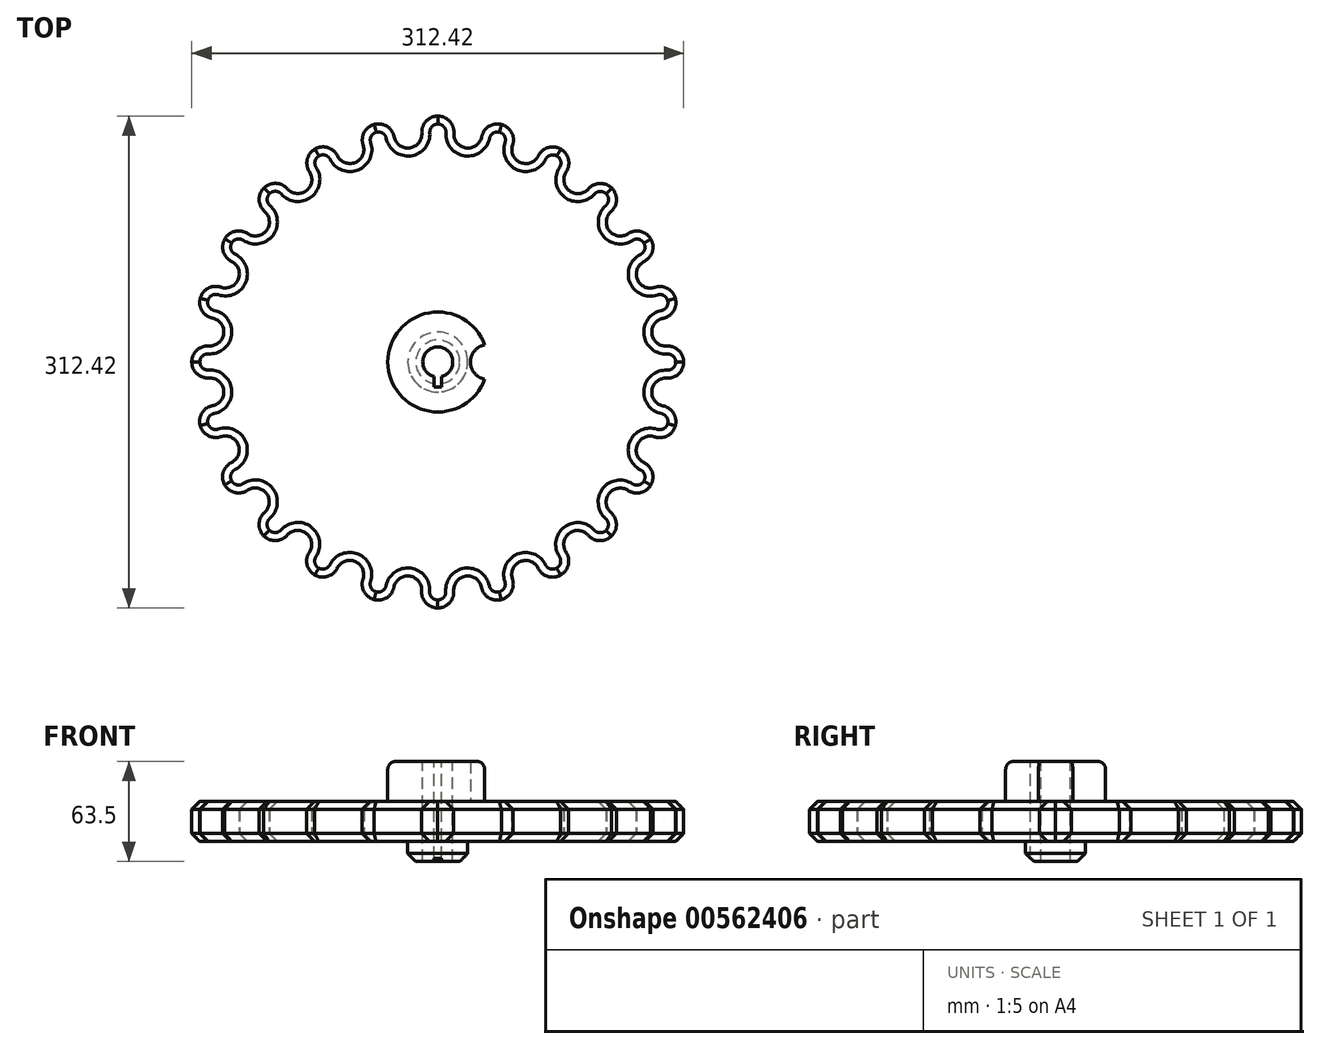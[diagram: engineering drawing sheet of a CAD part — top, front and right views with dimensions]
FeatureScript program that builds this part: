
annotation { "Feature Type Name" : "Feature", "Feature Type Description" : "" }
export const myFeature = defineFeature(function(context is Context, id is Id, definition is map)
    precondition{}
    {
        {
            var Q0;
            Q0=qCreatedBy(makeId("Top.planeOp"),FACE);
            var sketch = newSketch(context, id + "F0", { "sketchPlane" : qUnion([Q0])});
            skCircle(sketch, "E0", {"center": v(0, 0) * mm, "radius": 146.05 * mm, "construction": true});
            skArc(sketch, "E1", {"start": v(145.34, -10.14) * mm, "mid": v(156.2, -0.02) * mm, "end": v(145.39, 10.14) * mm});
            skArc(sketch, "E2", {"start": v(143.08, 27.73) * mm, "mid": v(150.91, 40.34) * mm, "end": v(137.8, 47.3) * mm});
            skArc(sketch, "E3", {"start": v(143.38, 27.78) * mm, "mid": v(136, 17.85) * mm, "end": v(145.7, 10.16) * mm});
            skLineSegment(sketch, "E4", {"start": v(0, 0) * mm, "end": v(138.14, 47.42) * mm});
            skLineSegment(sketch, "E5", {"start": v(0, 0) * mm, "end": v(145.7, -10.16) * mm});
            skSolve(sketch);
        }
        {
            var Q0;
            Q0 = qSketchRegion(id + "F0", true);
            extrude(context, id + "F1", {"entities" : qUnion([Q0]), "depth" : 25.4 * mm, "offsetDistance" : 25.4 * mm});
        }
        {
            var Q0;
            Q0=makeQuery(id+"F1.opExtrude","SWEPT_BODY",BODY,{"disambiguationData":[OSD([sQuery(id+"F0.wireOp",EDGE,"E1"),sQuery(id+"F0.wireOp",EDGE,"E2"),sQuery(id+"F0.wireOp",EDGE,"E3"),sQuery(id+"F0.wireOp",EDGE,"E4"),sQuery(id+"F0.wireOp",EDGE,"E5")])]});
            var Q1;
            Q1=makeQuery(id+"F1.opExtrude","SWEPT_EDGE",EDGE,{"disambiguationData":[OSD([sQuery(id+"F0.wireOp",EDGE,"E4"),sQuery(id+"F0.wireOp",EDGE,"E5")])]});
            circularPattern(context, id + "F2", {"operationType" : NewBodyOperationType.ADD, "entities" : qUnion([Q0]), "axis" : qUnion([Q1]), "angle" : 360 * degree, "instanceCount" : 24, "oppositeDirection" : true, "equalSpace" : true});
        }
        {
            var Q0;
            {var subQ0=makeQuery(id+"F1.opExtrude","CAP_FACE",FACE,{"disambiguationData":[OSD([sQuery(id+"F0.wireOp",EDGE,"E1"),sQuery(id+"F0.wireOp",EDGE,"E2"),sQuery(id+"F0.wireOp",EDGE,"E3"),sQuery(id+"F0.wireOp",EDGE,"E4"),sQuery(id+"F0.wireOp",EDGE,"E5")])],"isStart":false});Q0=makeQuery(id+"F2.boolean.opBoolean","MERGE",FACE,{"derivedFrom":[subQ0,makeQuery(id+"F2.opPattern","COPY",FACE,{"derivedFrom":subQ0,"instanceName":"1"}),makeQuery(id+"F2.opPattern","COPY",FACE,{"derivedFrom":subQ0,"instanceName":"2"}),makeQuery(id+"F2.opPattern","COPY",FACE,{"derivedFrom":subQ0,"instanceName":"3"}),makeQuery(id+"F2.opPattern","COPY",FACE,{"derivedFrom":subQ0,"instanceName":"4"}),makeQuery(id+"F2.opPattern","COPY",FACE,{"derivedFrom":subQ0,"instanceName":"5"}),makeQuery(id+"F2.opPattern","COPY",FACE,{"derivedFrom":subQ0,"instanceName":"6"}),makeQuery(id+"F2.opPattern","COPY",FACE,{"derivedFrom":subQ0,"instanceName":"7"}),makeQuery(id+"F2.opPattern","COPY",FACE,{"derivedFrom":subQ0,"instanceName":"8"}),makeQuery(id+"F2.opPattern","COPY",FACE,{"derivedFrom":subQ0,"instanceName":"9"}),makeQuery(id+"F2.opPattern","COPY",FACE,{"derivedFrom":subQ0,"instanceName":"10"}),makeQuery(id+"F2.opPattern","COPY",FACE,{"derivedFrom":subQ0,"instanceName":"11"}),makeQuery(id+"F2.opPattern","COPY",FACE,{"derivedFrom":subQ0,"instanceName":"12"}),makeQuery(id+"F2.opPattern","COPY",FACE,{"derivedFrom":subQ0,"instanceName":"13"}),makeQuery(id+"F2.opPattern","COPY",FACE,{"derivedFrom":subQ0,"instanceName":"14"}),makeQuery(id+"F2.opPattern","COPY",FACE,{"derivedFrom":subQ0,"instanceName":"15"}),makeQuery(id+"F2.opPattern","COPY",FACE,{"derivedFrom":subQ0,"instanceName":"16"}),makeQuery(id+"F2.opPattern","COPY",FACE,{"derivedFrom":subQ0,"instanceName":"17"}),makeQuery(id+"F2.opPattern","COPY",FACE,{"derivedFrom":subQ0,"instanceName":"18"}),makeQuery(id+"F2.opPattern","COPY",FACE,{"derivedFrom":subQ0,"instanceName":"19"}),makeQuery(id+"F2.opPattern","COPY",FACE,{"derivedFrom":subQ0,"instanceName":"20"}),makeQuery(id+"F2.opPattern","COPY",FACE,{"derivedFrom":subQ0,"instanceName":"21"}),makeQuery(id+"F2.opPattern","COPY",FACE,{"derivedFrom":subQ0,"instanceName":"22"}),makeQuery(id+"F2.opPattern","COPY",FACE,{"derivedFrom":subQ0,"instanceName":"23"})]});}
            var Q1;
            {var subQ0=makeQuery(id+"F1.opExtrude","CAP_FACE",FACE,{"disambiguationData":[OSD([sQuery(id+"F0.wireOp",EDGE,"E1"),sQuery(id+"F0.wireOp",EDGE,"E2"),sQuery(id+"F0.wireOp",EDGE,"E3"),sQuery(id+"F0.wireOp",EDGE,"E4"),sQuery(id+"F0.wireOp",EDGE,"E5")])],"isStart":true});Q1=makeQuery(id+"F2.boolean.opBoolean","MERGE",FACE,{"derivedFrom":[subQ0,makeQuery(id+"F2.opPattern","COPY",FACE,{"derivedFrom":subQ0,"instanceName":"1"}),makeQuery(id+"F2.opPattern","COPY",FACE,{"derivedFrom":subQ0,"instanceName":"2"}),makeQuery(id+"F2.opPattern","COPY",FACE,{"derivedFrom":subQ0,"instanceName":"3"}),makeQuery(id+"F2.opPattern","COPY",FACE,{"derivedFrom":subQ0,"instanceName":"4"}),makeQuery(id+"F2.opPattern","COPY",FACE,{"derivedFrom":subQ0,"instanceName":"5"}),makeQuery(id+"F2.opPattern","COPY",FACE,{"derivedFrom":subQ0,"instanceName":"6"}),makeQuery(id+"F2.opPattern","COPY",FACE,{"derivedFrom":subQ0,"instanceName":"7"}),makeQuery(id+"F2.opPattern","COPY",FACE,{"derivedFrom":subQ0,"instanceName":"8"}),makeQuery(id+"F2.opPattern","COPY",FACE,{"derivedFrom":subQ0,"instanceName":"9"}),makeQuery(id+"F2.opPattern","COPY",FACE,{"derivedFrom":subQ0,"instanceName":"10"}),makeQuery(id+"F2.opPattern","COPY",FACE,{"derivedFrom":subQ0,"instanceName":"11"}),makeQuery(id+"F2.opPattern","COPY",FACE,{"derivedFrom":subQ0,"instanceName":"12"}),makeQuery(id+"F2.opPattern","COPY",FACE,{"derivedFrom":subQ0,"instanceName":"13"}),makeQuery(id+"F2.opPattern","COPY",FACE,{"derivedFrom":subQ0,"instanceName":"14"}),makeQuery(id+"F2.opPattern","COPY",FACE,{"derivedFrom":subQ0,"instanceName":"15"}),makeQuery(id+"F2.opPattern","COPY",FACE,{"derivedFrom":subQ0,"instanceName":"16"}),makeQuery(id+"F2.opPattern","COPY",FACE,{"derivedFrom":subQ0,"instanceName":"17"}),makeQuery(id+"F2.opPattern","COPY",FACE,{"derivedFrom":subQ0,"instanceName":"18"}),makeQuery(id+"F2.opPattern","COPY",FACE,{"derivedFrom":subQ0,"instanceName":"19"}),makeQuery(id+"F2.opPattern","COPY",FACE,{"derivedFrom":subQ0,"instanceName":"20"}),makeQuery(id+"F2.opPattern","COPY",FACE,{"derivedFrom":subQ0,"instanceName":"21"}),makeQuery(id+"F2.opPattern","COPY",FACE,{"derivedFrom":subQ0,"instanceName":"22"}),makeQuery(id+"F2.opPattern","COPY",FACE,{"derivedFrom":subQ0,"instanceName":"23"})]});}
            chamfer(context, id + "F3", {"entities" : qUnion([Q0, Q1]), "width" : 5.08 * mm, "tangentPropagation" : true});
        }
        {
            var Q0;
            {var subQ0=makeQuery(id+"F1.opExtrude","CAP_FACE",FACE,{"disambiguationData":[OSD([sQuery(id+"F0.wireOp",EDGE,"E1"),sQuery(id+"F0.wireOp",EDGE,"E2"),sQuery(id+"F0.wireOp",EDGE,"E3"),sQuery(id+"F0.wireOp",EDGE,"E4"),sQuery(id+"F0.wireOp",EDGE,"E5")])],"isStart":false});Q0=makeQuery(id+"F2.boolean.opBoolean","MERGE",FACE,{"derivedFrom":[subQ0,makeQuery(id+"F2.opPattern","COPY",FACE,{"derivedFrom":subQ0,"instanceName":"1"}),makeQuery(id+"F2.opPattern","COPY",FACE,{"derivedFrom":subQ0,"instanceName":"2"}),makeQuery(id+"F2.opPattern","COPY",FACE,{"derivedFrom":subQ0,"instanceName":"3"}),makeQuery(id+"F2.opPattern","COPY",FACE,{"derivedFrom":subQ0,"instanceName":"4"}),makeQuery(id+"F2.opPattern","COPY",FACE,{"derivedFrom":subQ0,"instanceName":"5"}),makeQuery(id+"F2.opPattern","COPY",FACE,{"derivedFrom":subQ0,"instanceName":"6"}),makeQuery(id+"F2.opPattern","COPY",FACE,{"derivedFrom":subQ0,"instanceName":"7"}),makeQuery(id+"F2.opPattern","COPY",FACE,{"derivedFrom":subQ0,"instanceName":"8"}),makeQuery(id+"F2.opPattern","COPY",FACE,{"derivedFrom":subQ0,"instanceName":"9"}),makeQuery(id+"F2.opPattern","COPY",FACE,{"derivedFrom":subQ0,"instanceName":"10"}),makeQuery(id+"F2.opPattern","COPY",FACE,{"derivedFrom":subQ0,"instanceName":"11"}),makeQuery(id+"F2.opPattern","COPY",FACE,{"derivedFrom":subQ0,"instanceName":"12"}),makeQuery(id+"F2.opPattern","COPY",FACE,{"derivedFrom":subQ0,"instanceName":"13"}),makeQuery(id+"F2.opPattern","COPY",FACE,{"derivedFrom":subQ0,"instanceName":"14"}),makeQuery(id+"F2.opPattern","COPY",FACE,{"derivedFrom":subQ0,"instanceName":"15"}),makeQuery(id+"F2.opPattern","COPY",FACE,{"derivedFrom":subQ0,"instanceName":"16"}),makeQuery(id+"F2.opPattern","COPY",FACE,{"derivedFrom":subQ0,"instanceName":"17"}),makeQuery(id+"F2.opPattern","COPY",FACE,{"derivedFrom":subQ0,"instanceName":"18"}),makeQuery(id+"F2.opPattern","COPY",FACE,{"derivedFrom":subQ0,"instanceName":"19"}),makeQuery(id+"F2.opPattern","COPY",FACE,{"derivedFrom":subQ0,"instanceName":"20"}),makeQuery(id+"F2.opPattern","COPY",FACE,{"derivedFrom":subQ0,"instanceName":"21"}),makeQuery(id+"F2.opPattern","COPY",FACE,{"derivedFrom":subQ0,"instanceName":"22"}),makeQuery(id+"F2.opPattern","COPY",FACE,{"derivedFrom":subQ0,"instanceName":"23"})]});}
            var sketch = newSketch(context, id + "F4", { "sketchPlane" : qUnion([Q0])});
            skArc(sketch, "E6", {"start": v(29.83, 10.88) * mm, "mid": v(-31.75, 0) * mm, "end": v(29.83, -10.88) * mm});
            skArc(sketch, "E7", {"start": v(29.83, 10.88) * mm, "mid": v(20.7, 0) * mm, "end": v(29.83, -10.88) * mm});
            skSolve(sketch);
        }
        {
            var Q0;
            Q0 = qSketchRegion(id + "F4", true);
            extrude(context, id + "F5", {"entities" : qUnion([Q0]), "operationType" : NewBodyOperationType.ADD, "depth" : 25.4 * mm, "offsetDistance" : 25.4 * mm});
        }
        {
            var Q0;
            Q0=makeQuery(id+"F5.opExtrude","CAP_EDGE",EDGE,{"disambiguationData":[OSD([sQuery(id+"F4.wireOp",EDGE,"E6")])],"isStart":false});
            fillet(context, id + "F6", {"entities" : qUnion([Q0]), "radius" : 5.08 * mm, "tangentPropagation" : true, "allowEdgeOverflow" : false});
        }
        {
            var Q0;
            {var subQ0=makeQuery(id+"F1.opExtrude","CAP_FACE",FACE,{"disambiguationData":[OSD([sQuery(id+"F0.wireOp",EDGE,"E1"),sQuery(id+"F0.wireOp",EDGE,"E2"),sQuery(id+"F0.wireOp",EDGE,"E3"),sQuery(id+"F0.wireOp",EDGE,"E4"),sQuery(id+"F0.wireOp",EDGE,"E5")])],"isStart":true});Q0=makeQuery(id+"F2.boolean.opBoolean","MERGE",FACE,{"derivedFrom":[subQ0,makeQuery(id+"F2.opPattern","COPY",FACE,{"derivedFrom":subQ0,"instanceName":"1"}),makeQuery(id+"F2.opPattern","COPY",FACE,{"derivedFrom":subQ0,"instanceName":"2"}),makeQuery(id+"F2.opPattern","COPY",FACE,{"derivedFrom":subQ0,"instanceName":"3"}),makeQuery(id+"F2.opPattern","COPY",FACE,{"derivedFrom":subQ0,"instanceName":"4"}),makeQuery(id+"F2.opPattern","COPY",FACE,{"derivedFrom":subQ0,"instanceName":"5"}),makeQuery(id+"F2.opPattern","COPY",FACE,{"derivedFrom":subQ0,"instanceName":"6"}),makeQuery(id+"F2.opPattern","COPY",FACE,{"derivedFrom":subQ0,"instanceName":"7"}),makeQuery(id+"F2.opPattern","COPY",FACE,{"derivedFrom":subQ0,"instanceName":"8"}),makeQuery(id+"F2.opPattern","COPY",FACE,{"derivedFrom":subQ0,"instanceName":"9"}),makeQuery(id+"F2.opPattern","COPY",FACE,{"derivedFrom":subQ0,"instanceName":"10"}),makeQuery(id+"F2.opPattern","COPY",FACE,{"derivedFrom":subQ0,"instanceName":"11"}),makeQuery(id+"F2.opPattern","COPY",FACE,{"derivedFrom":subQ0,"instanceName":"12"}),makeQuery(id+"F2.opPattern","COPY",FACE,{"derivedFrom":subQ0,"instanceName":"13"}),makeQuery(id+"F2.opPattern","COPY",FACE,{"derivedFrom":subQ0,"instanceName":"14"}),makeQuery(id+"F2.opPattern","COPY",FACE,{"derivedFrom":subQ0,"instanceName":"15"}),makeQuery(id+"F2.opPattern","COPY",FACE,{"derivedFrom":subQ0,"instanceName":"16"}),makeQuery(id+"F2.opPattern","COPY",FACE,{"derivedFrom":subQ0,"instanceName":"17"}),makeQuery(id+"F2.opPattern","COPY",FACE,{"derivedFrom":subQ0,"instanceName":"18"}),makeQuery(id+"F2.opPattern","COPY",FACE,{"derivedFrom":subQ0,"instanceName":"19"}),makeQuery(id+"F2.opPattern","COPY",FACE,{"derivedFrom":subQ0,"instanceName":"20"}),makeQuery(id+"F2.opPattern","COPY",FACE,{"derivedFrom":subQ0,"instanceName":"21"}),makeQuery(id+"F2.opPattern","COPY",FACE,{"derivedFrom":subQ0,"instanceName":"22"}),makeQuery(id+"F2.opPattern","COPY",FACE,{"derivedFrom":subQ0,"instanceName":"23"})]});}
            var sketch = newSketch(context, id + "F7", { "sketchPlane" : qUnion([Q0])});
            skCircle(sketch, "E8", {"center": v(0, 0) * mm, "radius": 19.05 * mm});
            skSolve(sketch);
        }
        {
            var Q0;
            Q0 = qSketchRegion(id + "F7", true);
            extrude(context, id + "F8", {"entities" : qUnion([Q0]), "operationType" : NewBodyOperationType.ADD, "depth" : 12.7 * mm, "offsetDistance" : 25.4 * mm});
        }
        {
            var Q0;
            Q0=makeQuery(id+"F8.opExtrude","CAP_EDGE",EDGE,{"disambiguationData":[OSD([sQuery(id+"F7.wireOp",EDGE,"E8")])],"isStart":false});
            chamfer(context, id + "F9", {"entities" : qUnion([Q0]), "width" : 5.08 * mm, "tangentPropagation" : true});
        }
        {
            var Q0;
            Q0=makeQuery(id+"F5.opExtrude","CAP_FACE",FACE,{"disambiguationData":[OSD([sQuery(id+"F4.wireOp",EDGE,"E6"),sQuery(id+"F4.wireOp",EDGE,"E7")])],"isStart":false});
            var sketch = newSketch(context, id + "F10", { "sketchPlane" : qUnion([Q0])});
            skArc(sketch, "E9", {"start": v(2.39, -9.22) * mm, "mid": v(0, 9.52) * mm, "end": v(-2.39, -9.22) * mm});
            skLineSegment(sketch, "E10.bottom", {"start": v(-2.39, 0) * mm, "end": v(2.39, 0) * mm, "construction": true});
            skLineSegment(sketch, "E10.top", {"start": v(-2.39, -15.88) * mm, "end": v(2.39, -15.88) * mm});
            skLineSegment(sketch, "E10.left", {"start": v(-2.39, -9.22) * mm, "end": v(-2.39, -15.88) * mm});
            skLineSegment(sketch, "E10.right", {"start": v(2.39, -9.22) * mm, "end": v(2.39, -15.88) * mm});
            skSolve(sketch);
        }
        {
            var Q0;
            Q0 = qSketchRegion(id + "F10", true);
            extrude(context, id + "F11", {"entities" : qUnion([Q0]), "operationType" : NewBodyOperationType.REMOVE, "endBound" : BoundingType.THROUGH_ALL, "oppositeDirection" : true, "depth" : 25.4 * mm, "offsetDistance" : 25.4 * mm});
        }
    });
